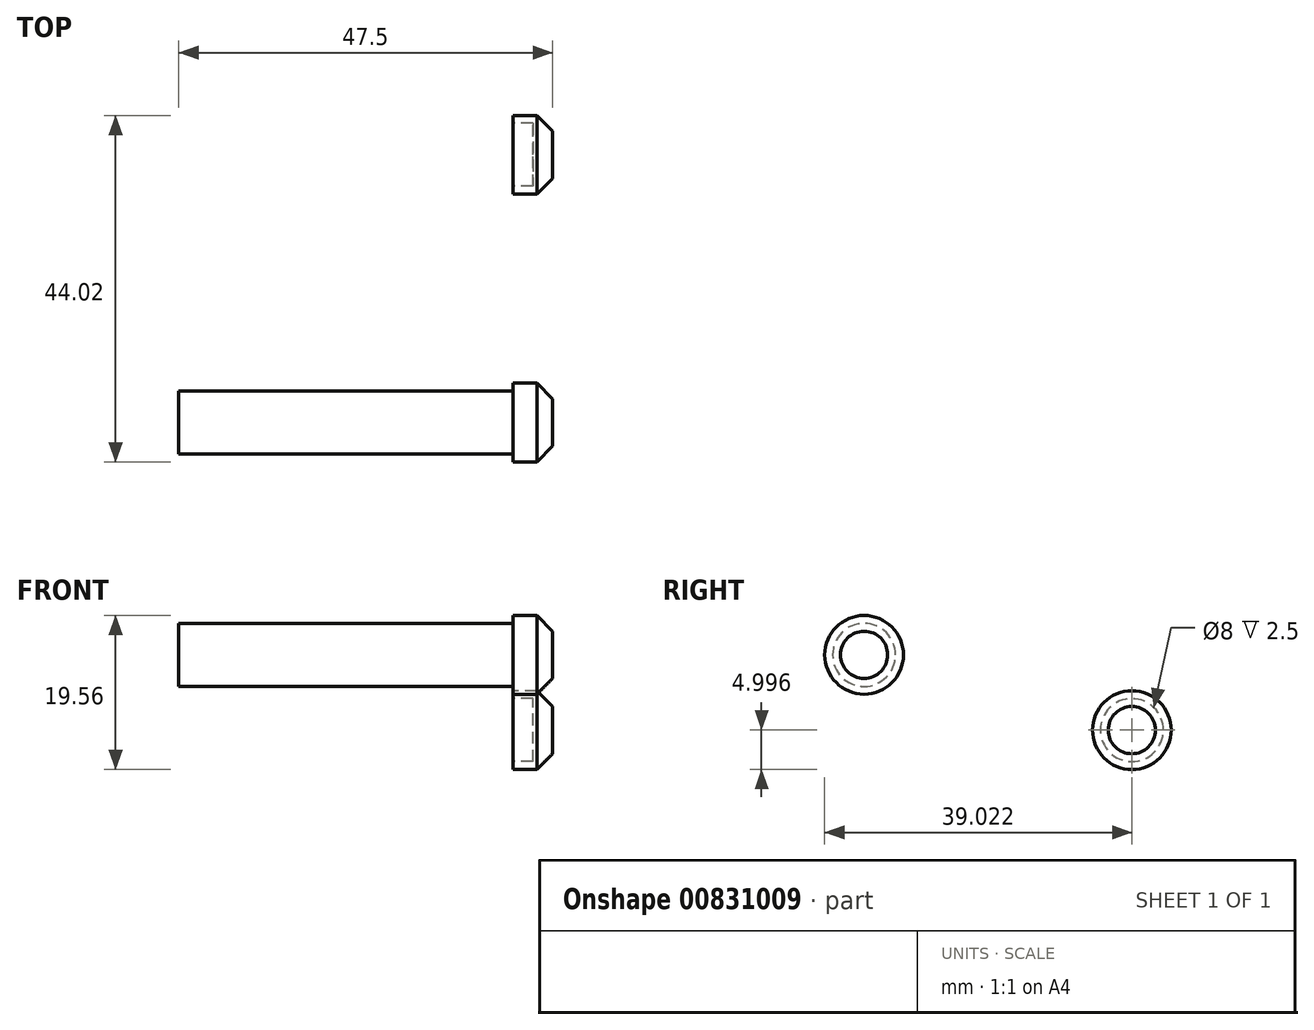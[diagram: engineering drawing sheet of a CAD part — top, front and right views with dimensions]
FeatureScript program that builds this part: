
annotation { "Feature Type Name" : "Feature", "Feature Type Description" : "" }
export const myFeature = defineFeature(function(context is Context, id is Id, definition is map)
    precondition{}
    {
        {
            var Q0;
            Q0=qCreatedBy(makeId("Right.planeOp"),FACE);
            var sketch = newSketch(context, id + "F0", { "sketchPlane" : qUnion([Q0])});
            skCircle(sketch, "E0", {"center": v(-45.42, 26.55) * mm, "radius": 4 * mm});
            skCircle(sketch, "E1", {"center": v(-45.42, 26.55) * mm, "radius": 5 * mm});
            skSolve(sketch);
        }
        {
            var Q0;
            Q0=makeQuery(id+"F0.imprint","IMPRINT",FACE,{"disambiguationData":[TD([[makeQuery(id+"F0.imprint","IMPRINT",EDGE,{"derivedFrom":sQuery(id+"F0.wireOp",EDGE,"E0")}),1.0]])]});
            extrude(context, id + "F1", {"entities" : qUnion([Q0]), "oppositeDirection" : true, "depth" : 42.5 * mm, "offsetDistance" : 25 * mm});
        }
        {
            var Q0;
            Q0 = qSketchRegion(id + "F0", true);
            var Q1;
            Q1=makeQuery(id+"F1.opExtrude","CAP_FACE",FACE,{"disambiguationData":[OSD([sQuery(id+"F0.wireOp",EDGE,"E0")])],"isStart":true});
            extrude(context, id + "F2", {"entities" : qUnion([Q0, Q1]), "operationType" : NewBodyOperationType.ADD, "depth" : 5 * mm, "offsetDistance" : 25 * mm});
        }
        {
            var Q0;
            Q0=makeQuery(id+"F2.opExtrude","CAP_EDGE",EDGE,{"disambiguationData":[OSD([sQuery(id+"F0.wireOp",EDGE,"E1")])],"isStart":false});
            chamfer(context, id + "F3", {"entities" : qUnion([Q0]), "width" : 2 * mm, "tangentPropagation" : true});
        }
        {
            var Q0;
            Q0=qCreatedBy(makeId("Right.planeOp"),FACE);
            var sketch = newSketch(context, id + "F4", { "sketchPlane" : qUnion([Q0])});
            skCircle(sketch, "E2", {"center": v(-11.4, 16.99) * mm, "radius": 4 * mm});
            skCircle(sketch, "E3", {"center": v(-11.4, 16.99) * mm, "radius": 5 * mm});
            skSolve(sketch);
        }
        {
            var Q0;
            Q0=makeQuery(id+"F4.imprint","IMPRINT",FACE,{"disambiguationData":[TD([[makeQuery(id+"F4.imprint","IMPRINT",EDGE,{"derivedFrom":sQuery(id+"F4.wireOp",EDGE,"E2")}),-1.0]])]});
            var Q1;
            Q1=makeQuery(id+"F4.imprint","IMPRINT",FACE,{"disambiguationData":[TD([[makeQuery(id+"F4.imprint","IMPRINT",EDGE,{"derivedFrom":sQuery(id+"F4.wireOp",EDGE,"E2")}),1.0]])]});
            extrude(context, id + "F5", {"entities" : qUnion([Q0, Q1]), "depth" : 5 * mm, "offsetDistance" : 25 * mm});
        }
        {
            var Q0;
            Q0=makeQuery(id+"F4.imprint","IMPRINT",FACE,{"disambiguationData":[TD([[makeQuery(id+"F4.imprint","IMPRINT",EDGE,{"derivedFrom":sQuery(id+"F4.wireOp",EDGE,"E2")}),1.0]])]});
            extrude(context, id + "F6", {"entities" : qUnion([Q0]), "operationType" : NewBodyOperationType.REMOVE, "depth" : 2.5 * mm, "offsetDistance" : 25 * mm});
        }
        {
            var Q0;
            Q0=makeQuery(id+"F5.opExtrude","CAP_EDGE",EDGE,{"disambiguationData":[OSD([sQuery(id+"F4.wireOp",EDGE,"E3")])],"isStart":false});
            chamfer(context, id + "F7", {"entities" : qUnion([Q0]), "width" : 2 * mm, "tangentPropagation" : true});
        }
    });
